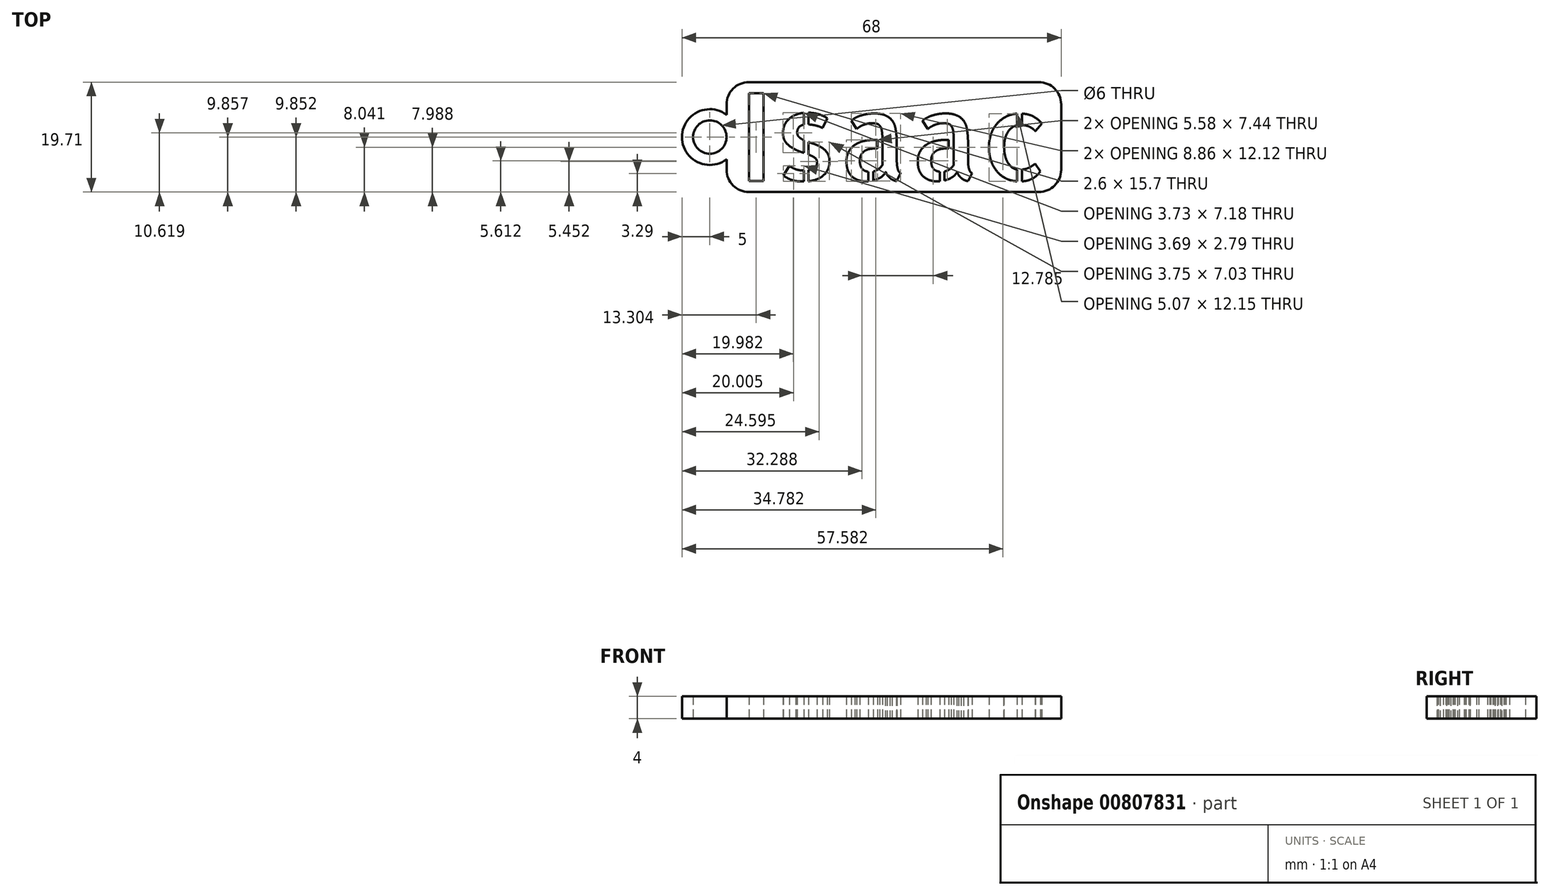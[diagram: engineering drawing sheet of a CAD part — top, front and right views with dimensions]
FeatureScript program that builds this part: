
annotation { "Feature Type Name" : "Feature", "Feature Type Description" : "" }
export const myFeature = defineFeature(function(context is Context, id is Id, definition is map)
    precondition{}
    {
        {
            var Q0;
            Q0=qCreatedBy(makeId("Top.planeOp"),FACE);
            var sketch = newSketch(context, id + "F0", { "sketchPlane" : qUnion([Q0])});
            skLineSegment(sketch, "E0.bottom", {"start": v(-2, -2) * mm, "end": v(58, -2) * mm});
            skLineSegment(sketch, "E0.top", {"start": v(-2, 17.71) * mm, "end": v(58, 17.71) * mm});
            skLineSegment(sketch, "E0.left", {"start": v(-2, -2) * mm, "end": v(-2, 3.86) * mm});
            skLineSegment(sketch, "E0.right", {"start": v(58, -2) * mm, "end": v(58, 17.71) * mm});
            skArc(sketch, "E1", {"start": v(-2, 11.86) * mm, "mid": v(-10, 7.86) * mm, "end": v(-2, 3.86) * mm});
            skLineSegment(sketch, "E2.trimOffspring", {"start": v(-2, 11.86) * mm, "end": v(-2, 17.71) * mm});
            skCircle(sketch, "E3", {"center": v(-5, 7.86) * mm, "radius": 3 * mm});
            skText(sketch, "E4", { "text": "Isaac", "fontName": "AllertaStencil-Regular.ttf"});
            skLineSegment(sketch, "E5", {"start": v(58, 7.86) * mm, "end": v(-10, 7.86) * mm, "construction": true});
            const initialGuessF0  = {"E4": [0, 0, 1, 0, 0.01571]};
            skSetInitialGuess(sketch, initialGuessF0);
            skSolve(sketch);
        }
        {
            var Q0;
            Q0=makeQuery(id+"F0.imprint","IMPRINT",FACE,{"disambiguationData":[TD([[makeQuery(id+"F0.imprint","IMPRINT",EDGE,{"derivedFrom":sQuery(id+"F0.wireOp",EDGE,"E0.bottom")}),1.0]])]});
            extrude(context, id + "F1", {"entities" : qUnion([Q0]), "depth" : 4 * mm, "offsetDistance" : 25 * mm});
        }
        {
            var Q0;
            Q0=makeQuery(id+"F1.opExtrude","SWEPT_EDGE",EDGE,{"disambiguationData":[OSD([sQuery(id+"F0.wireOp",EDGE,"E0.bottom"),sQuery(id+"F0.wireOp",EDGE,"E0.left")])]});
            var Q1;
            Q1=makeQuery(id+"F1.opExtrude","SWEPT_EDGE",EDGE,{"disambiguationData":[OSD([sQuery(id+"F0.wireOp",EDGE,"E0.bottom"),sQuery(id+"F0.wireOp",EDGE,"E0.right")])]});
            var Q2;
            Q2=makeQuery(id+"F1.opExtrude","SWEPT_EDGE",EDGE,{"disambiguationData":[OSD([sQuery(id+"F0.wireOp",EDGE,"E0.top"),sQuery(id+"F0.wireOp",EDGE,"E0.right")])]});
            var Q3;
            Q3=makeQuery(id+"F1.opExtrude","SWEPT_EDGE",EDGE,{"disambiguationData":[OSD([sQuery(id+"F0.wireOp",EDGE,"E0.top"),sQuery(id+"F0.wireOp",EDGE,"E2.trimOffspring")])]});
            fillet(context, id + "F2", {"entities" : qUnion([Q0, Q1, Q2, Q3]), "radius" : 4 * mm, "tangentPropagation" : true, "allowEdgeOverflow" : false});
        }
    });
